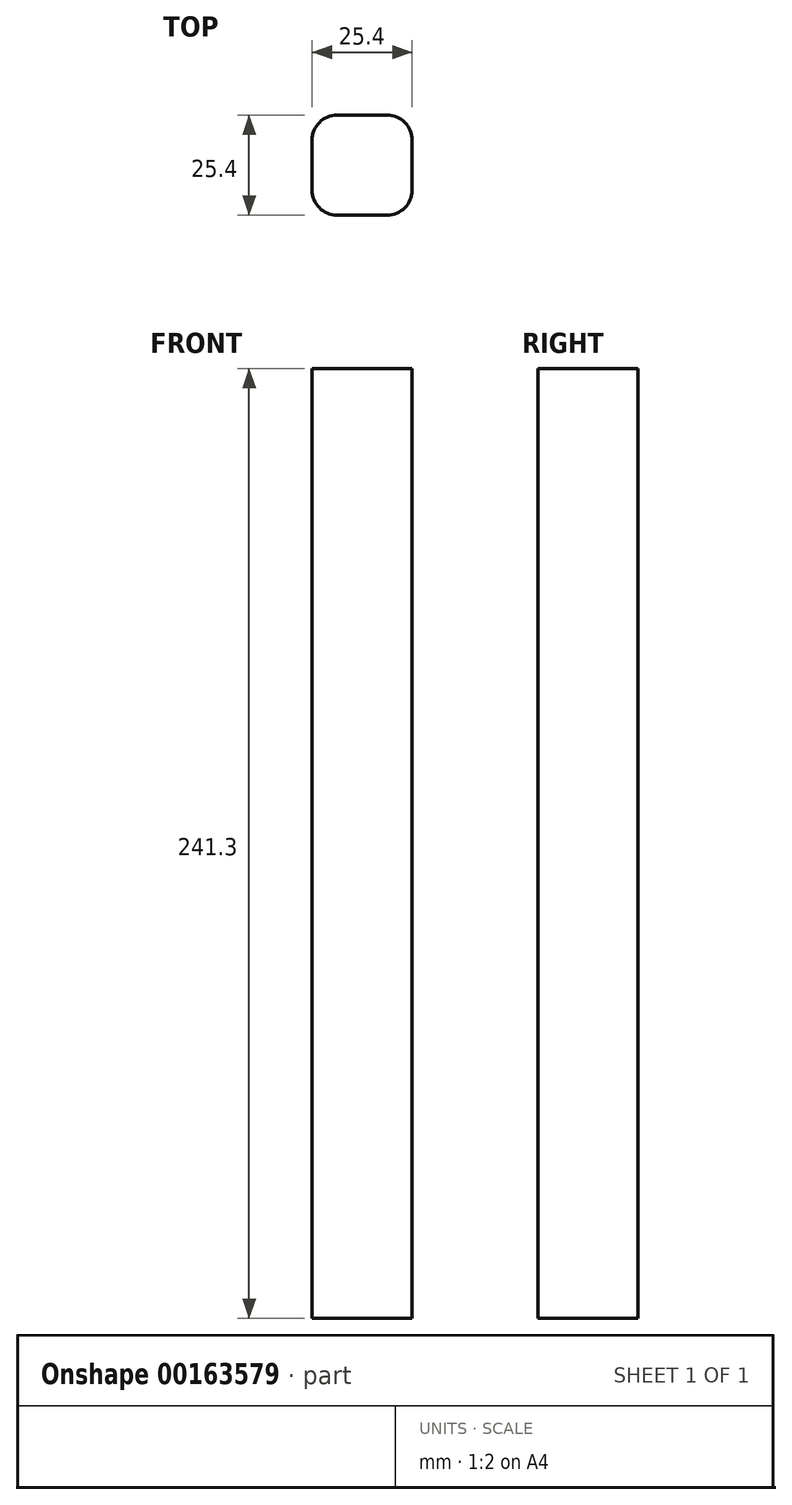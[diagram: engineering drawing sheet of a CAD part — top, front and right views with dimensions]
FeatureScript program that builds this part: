
annotation { "Feature Type Name" : "Feature", "Feature Type Description" : "" }
export const myFeature = defineFeature(function(context is Context, id is Id, definition is map)
    precondition{}
    {
        {
            var Q0;
            Q0=qCreatedBy(makeId("Top.planeOp"),FACE);
            var sketch = newSketch(context, id + "F0", { "sketchPlane" : qUnion([Q0])});
            skLineSegment(sketch, "E0.bottom", {"start": v(6.35, 12.7) * mm, "end": v(-6.35, 12.7) * mm});
            skLineSegment(sketch, "E0.top", {"start": v(6.35, -12.7) * mm, "end": v(-6.35, -12.7) * mm});
            skLineSegment(sketch, "E0.left", {"start": v(12.7, 6.35) * mm, "end": v(12.7, -6.35) * mm});
            skLineSegment(sketch, "E0.right", {"start": v(-12.7, 6.35) * mm, "end": v(-12.7, -6.35) * mm});
            skPoint(sketch, "E0.middle", {"position": v(0, 0) * mm});
            skPoint(sketch, "E1.visualSharp", {"position": v(-12.7, 12.7) * mm});
            skArc(sketch, "E1.filletArc", {"start": v(-6.35, 12.7) * mm, "mid": v(-10.84, 10.84) * mm, "end": v(-12.7, 6.35) * mm});
            skPoint(sketch, "E2.visualSharp", {"position": v(-12.7, -12.7) * mm});
            skArc(sketch, "E2.filletArc", {"start": v(-12.7, -6.35) * mm, "mid": v(-10.84, -10.84) * mm, "end": v(-6.35, -12.7) * mm});
            skPoint(sketch, "E3.visualSharp", {"position": v(12.7, -12.7) * mm});
            skArc(sketch, "E3.filletArc", {"start": v(6.35, -12.7) * mm, "mid": v(10.84, -10.84) * mm, "end": v(12.7, -6.35) * mm});
            skPoint(sketch, "E4.visualSharp", {"position": v(12.7, 12.7) * mm});
            skArc(sketch, "E4.filletArc", {"start": v(12.7, 6.35) * mm, "mid": v(10.84, 10.84) * mm, "end": v(6.35, 12.7) * mm});
            skSolve(sketch);
        }
        {
            var Q0;
            Q0=qSketchRegion(id+"F0",true);
            extrude(context, id + "F1", {"entities" : qUnion([Q0]), "depth" : 241.3 * mm, "offsetDistance" : 25.4 * mm});
        }
    });
